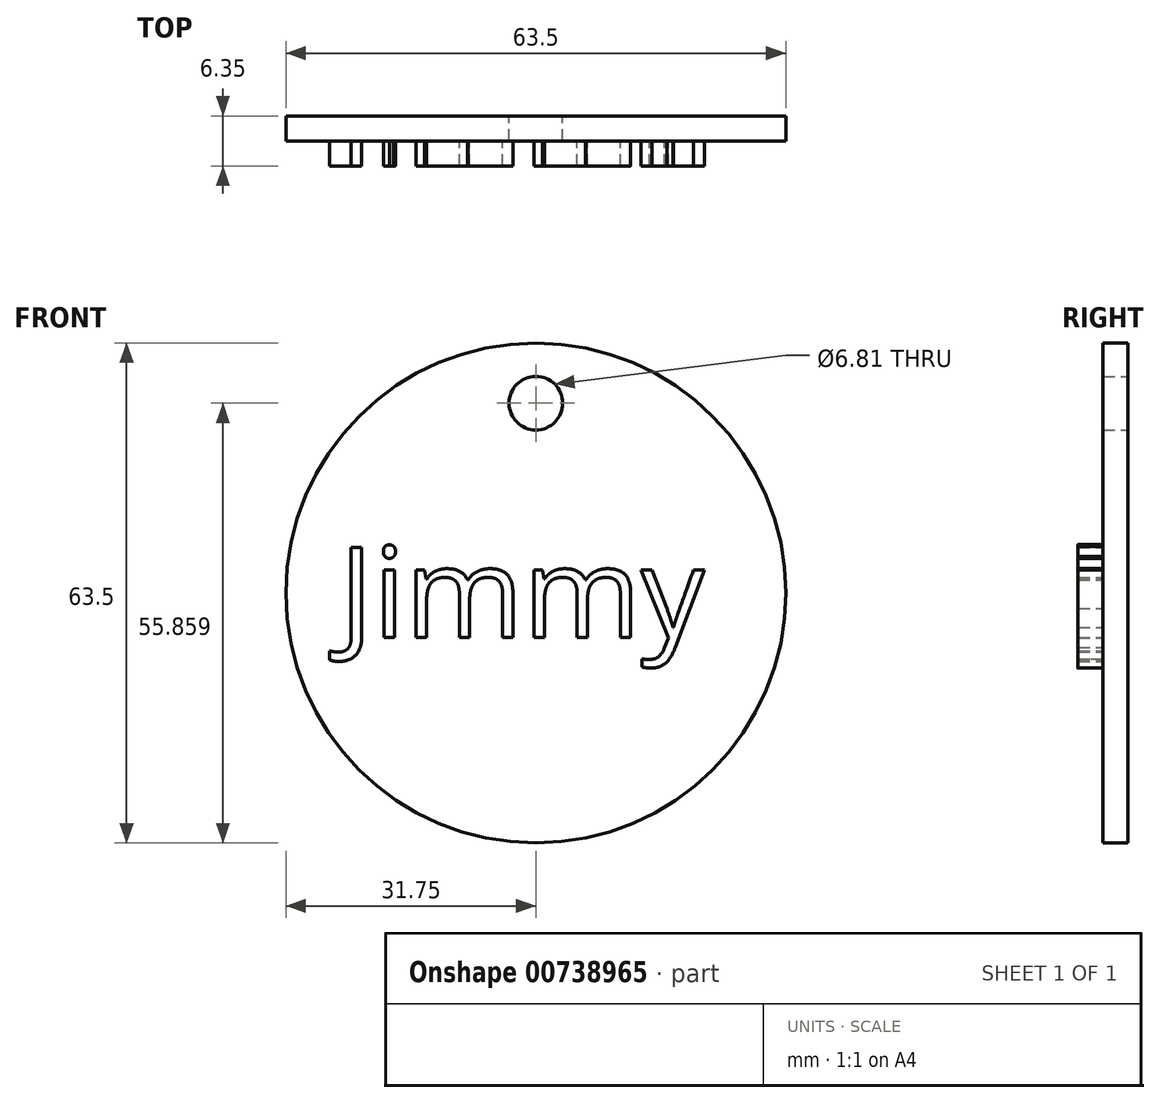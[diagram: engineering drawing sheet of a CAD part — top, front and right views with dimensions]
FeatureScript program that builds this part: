
annotation { "Feature Type Name" : "Feature", "Feature Type Description" : "" }
export const myFeature = defineFeature(function(context is Context, id is Id, definition is map)
    precondition{}
    {
        {
            var Q0;
            Q0=qCreatedBy(makeId("Front.planeOp"),FACE);
            var sketch = newSketch(context, id + "F0", { "sketchPlane" : qUnion([Q0])});
            skCircle(sketch, "E0", {"center": v(0, 0) * mm, "radius": 31.75 * mm});
            skSolve(sketch);
        }
        {
            var Q0;
            Q0 = qSketchRegion(id + "F0", true);
            extrude(context, id + "F1", {"entities" : qUnion([Q0]), "depth" : 3.17 * mm, "offsetDistance" : 25.4 * mm});
        }
        {
            var Q0;
            Q0=makeQuery(id+"F1.opExtrude","CAP_FACE",FACE,{"disambiguationData":[OSD([sQuery(id+"F0.wireOp",EDGE,"E0")])],"isStart":false});
            var sketch = newSketch(context, id + "F2", { "sketchPlane" : qUnion([Q0])});
            skText(sketch, "E1", { "text": "Jimmy", "fontName": "OpenSans-Regular.ttf"});
            const initialGuessF2  = {"E1": [-0.02494, -0.00567, 1, 0, 0.01158]};
            skSetInitialGuess(sketch, initialGuessF2);
            skSolve(sketch);
        }
        {
            var Q0;
            Q0 = qSketchRegion(id + "F2", true);
            extrude(context, id + "F3", {"entities" : qUnion([Q0]), "operationType" : NewBodyOperationType.ADD, "depth" : 3.17 * mm, "offsetDistance" : 25.4 * mm});
        }
        {
            var Q0;
            Q0=makeQuery(id+"F1.opExtrude","CAP_FACE",FACE,{"disambiguationData":[OSD([sQuery(id+"F0.wireOp",EDGE,"E0")])],"isStart":false});
            var sketch = newSketch(context, id + "F4", { "sketchPlane" : qUnion([Q0])});
            skCircle(sketch, "E2", {"center": v(0, 24.1) * mm, "radius": 3.4 * mm});
            skSolve(sketch);
        }
        {
            var Q0;
            Q0 = qSketchRegion(id + "F4", true);
            extrude(context, id + "F5", {"entities" : qUnion([Q0]), "operationType" : NewBodyOperationType.REMOVE, "endBound" : BoundingType.SYMMETRIC, "depth" : 25.4 * mm, "offsetDistance" : 25.4 * mm});
        }
    });
